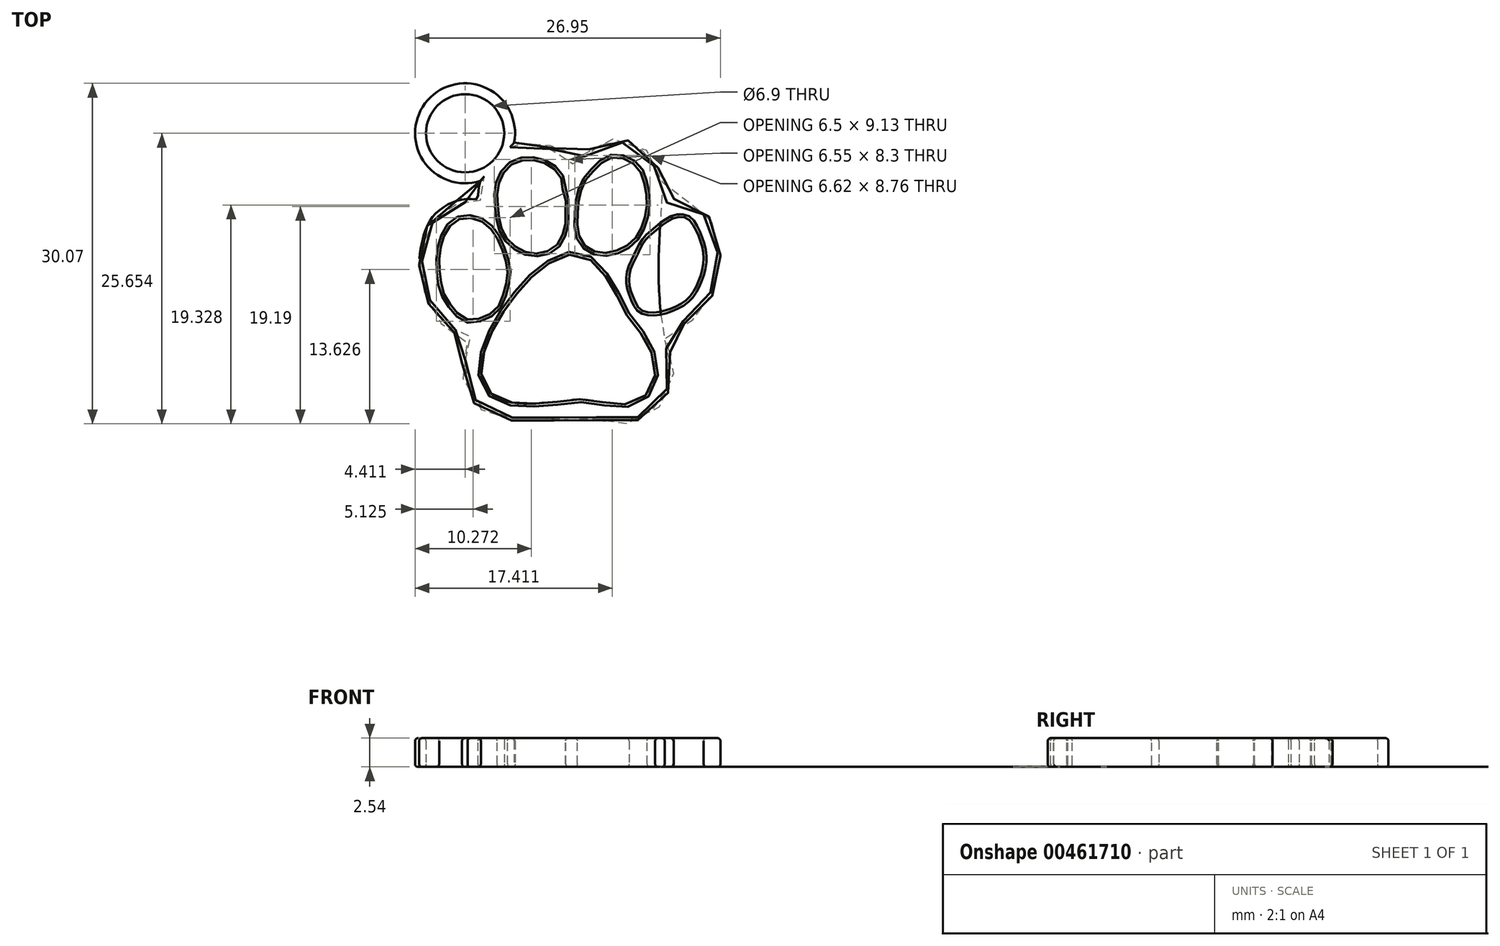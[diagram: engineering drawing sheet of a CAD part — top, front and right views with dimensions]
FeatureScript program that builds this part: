
annotation { "Feature Type Name" : "Feature", "Feature Type Description" : "" }
export const myFeature = defineFeature(function(context is Context, id is Id, definition is map)
    precondition{}
    {
        {
            var Q0;
            Q0=qCreatedBy(makeId("Top.planeOp"),FACE);
            var sketch = newSketch(context, id + "F0", { "sketchPlane" : qUnion([Q0])});
            skPoint(sketch, "E0.middle", {"position": v(0, 0) * mm});
            skFitSpline(sketch, "E1", {"points": [v(0.8, 9.25) * mm, v(1.85, 10.08) * mm, v(3.3, 10.95) * mm, v(5.35, 11.07) * mm, v(7.02, 10.27) * mm, v(7.95, 9.06) * mm, v(8.63, 7.14) * mm, v(8.78, 6) * mm, v(8.78, 5.81) * mm, v(8.94, 5.81) * mm, v(10.18, 5.86) * mm, v(11.2, 5.64) * mm, v(12.22, 4.87) * mm, v(13.49, 2.43) * mm, v(13.55, -0.42) * mm, v(12.76, -3.12) * mm, v(11.25, -4.79) * mm, v(8.86, -5.83) * mm, v(8.78, -5.89) * mm, v(8.75, -6) * mm, v(8.78, -6.12) * mm, v(9.33, -8) * mm, v(9.43, -10.3) * mm, v(8.29, -12.48) * mm, v(7.72, -12.95) * mm, v(5.95, -13.83) * mm, v(4.02, -13.93) * mm, v(2.72, -13.67) * mm, v(1.9, -13.47) * mm, v(1.68, -13.47) * mm, v(0.61, -13.46) * mm, v(-0.31, -13.62) * mm, v(-1.11, -13.7) * mm, v(-1.96, -13.74) * mm, v(-3.44, -13.74) * mm, v(-4.2, -13.74) * mm, v(-5.71, -13.5) * mm, v(-7.8, -12.45) * mm, v(-8.8, -10.88) * mm, v(-9.12, -9.52) * mm, v(-9, -7.92) * mm, v(-8.68, -6.67) * mm, v(-8.66, -6.47) * mm, v(-8.66, -6.36) * mm, v(-8.88, -6.29) * mm, v(-10.37, -5.63) * mm, v(-11.93, -3.75) * mm, v(-12.87, -0.69) * mm, v(-12.76, 1.66) * mm, v(-12.09, 3.74) * mm, v(-11.12, 4.89) * mm, v(-9.37, 5.76) * mm, v(-7.97, 5.85) * mm, v(-7.85, 5.85) * mm, v(-7.73, 5.91) * mm, v(-7.73, 6.16) * mm, v(-7.54, 7.43) * mm, v(-6.9, 9.1) * mm, v(-5.5, 10.36) * mm, v(-3.78, 11) * mm, v(-1.74, 10.72) * mm, v(-0.62, 10.12) * mm, v(0.43, 9.4) * mm, v(0.57, 9.28) * mm, v(0.64, 9.23) * mm, v(0.7, 9.22) * mm, v(0.74, 9.22) * mm, v(0.8, 9.25) * mm]});
            skFitSpline(sketch, "E2", {"points": [v(0.35, 0.93) * mm, v(1.28, 0.88) * mm, v(2.22, 0.47) * mm, v(3.36, -0.73) * mm, v(4.4, -2.4) * mm, v(5.08, -3.75) * mm, v(5.65, -4.79) * mm, v(6.43, -5.78) * mm, v(7, -6.35) * mm, v(7.32, -6.92) * mm, v(7.84, -8.74) * mm, v(7.79, -10.35) * mm, v(6.9, -11.6) * mm, v(5.63, -12.17) * mm, v(4.66, -12.3) * mm, v(3.2, -12.05) * mm, v(2.13, -11.86) * mm, v(1.32, -11.82) * mm, v(0.34, -11.86) * mm, v(-0.52, -12.03) * mm, v(-1.47, -12.1) * mm, v(-2.89, -12.2) * mm, v(-4.58, -12.13) * mm, v(-6.33, -11.52) * mm, v(-7.2, -10.45) * mm, v(-7.48, -9.1) * mm, v(-7.07, -7.27) * mm, v(-6.13, -5.12) * mm, v(-4.5, -2.75) * mm, v(-2.68, -0.75) * mm, v(-0.8, 0.6) * mm, v(-0.27, 0.81) * mm, v(0.14, 0.88) * mm, v(0.35, 0.93) * mm]});
            skFitSpline(sketch, "E3", {"points": [v(9.5, 4.18) * mm, v(10.39, 4.26) * mm, v(11.07, 3.86) * mm, v(11.83, 2.37) * mm, v(12.2, 0.65) * mm, v(11.91, -0.92) * mm, v(11.03, -2.68) * mm, v(9.43, -3.77) * mm, v(7.54, -4.17) * mm, v(6.54, -3.85) * mm, v(6.14, -3.16) * mm, v(5.7, -2.04) * mm, v(5.7, -0.48) * mm, v(6.26, 0.77) * mm, v(6.94, 2.1) * mm, v(8.26, 3.33) * mm, v(8.94, 3.86) * mm, v(9.2, 4) * mm, v(9.38, 4.1) * mm, v(9.46, 4.14) * mm, v(9.5, 4.18) * mm]});
            skFitSpline(sketch, "E4", {"points": [v(1.79, 7.53) * mm, v(3, 8.88) * mm, v(4.48, 9.56) * mm, v(5.95, 9.02) * mm, v(6.7, 8.08) * mm, v(7.17, 6.05) * mm, v(7.06, 4.44) * mm, v(6.28, 2.57) * mm, v(5.14, 1.58) * mm, v(3.58, 1.11) * mm, v(2.12, 1.42) * mm, v(1.18, 2.62) * mm, v(1.08, 4.8) * mm, v(1.23, 6.16) * mm, v(1.54, 7.06) * mm, v(1.69, 7.35) * mm, v(1.79, 7.53) * mm]});
            skFitSpline(sketch, "E5", {"points": [v(-4.76, 8.9) * mm, v(-3.93, 9.25) * mm, v(-2.57, 9.25) * mm, v(-1.43, 8.8) * mm, v(-0.6, 8.07) * mm, v(-0.28, 7.3) * mm, v(-0.23, 6.62) * mm, v(0, 5.81) * mm, v(0, 5.1) * mm, v(0, 3.76) * mm, v(-0.23, 2.77) * mm, v(-0.8, 1.78) * mm, v(-2.16, 1.1) * mm, v(-3.72, 1.26) * mm, v(-5.12, 2.3) * mm, v(-5.7, 3.4) * mm, v(-5.95, 5) * mm, v(-6, 6.67) * mm, v(-5.6, 7.97) * mm, v(-5.12, 8.6) * mm, v(-4.93, 8.74) * mm, v(-4.76, 8.9) * mm]});
            skFitSpline(sketch, "E6", {"points": [v(-10.2, 3.48) * mm, v(-9.4, 4.08) * mm, v(-7.92, 4.08) * mm, v(-6.5, 3.14) * mm, v(-5.55, 1.25) * mm, v(-5.12, -0.69) * mm, v(-5.42, -2.33) * mm, v(-6.03, -3.75) * mm, v(-7.07, -4.48) * mm, v(-8.66, -4.79) * mm, v(-9.94, -3.75) * mm, v(-10.82, -2.26) * mm, v(-11.15, 0) * mm, v(-11.02, 1.65) * mm, v(-10.56, 2.98) * mm, v(-10.4, 3.2) * mm, v(-10.2, 3.48) * mm]});
            skArc(sketch, "E7", {"start": v(-4.53, 10.84) * mm, "mid": v(-12.17, 14.6) * mm, "end": v(-7.53, 7.46) * mm});
            skCircle(sketch, "E8", {"center": v(-8.87, 11.66) * mm, "radius": 3.45 * mm});
            skSolve(sketch);
        }
        {
            var Q0;
            Q0 = qSketchRegion(id + "F0", true);
            extrude(context, id + "F1", {"entities" : qUnion([Q0]), "depth" : 2.54 * mm});
        }
        {
            var Q0;
            Q0=makeQuery(id+"F1.opExtrude","CAP_FACE",FACE,{"disambiguationData":[OSD([sQuery(id+"F0.wireOp",EDGE,"E1"),sQuery(id+"F0.wireOp",EDGE,"E2"),sQuery(id+"F0.wireOp",EDGE,"E3"),sQuery(id+"F0.wireOp",EDGE,"E4"),sQuery(id+"F0.wireOp",EDGE,"E5"),sQuery(id+"F0.wireOp",EDGE,"E6"),sQuery(id+"F0.wireOp",EDGE,"E7"),sQuery(id+"F0.wireOp",EDGE,"E8")])],"isStart":false});
            var Q1;
            Q1=makeQuery(id+"F1.opExtrude","CAP_FACE",FACE,{"disambiguationData":[OSD([sQuery(id+"F0.wireOp",EDGE,"E1"),sQuery(id+"F0.wireOp",EDGE,"E2"),sQuery(id+"F0.wireOp",EDGE,"E3"),sQuery(id+"F0.wireOp",EDGE,"E4"),sQuery(id+"F0.wireOp",EDGE,"E5"),sQuery(id+"F0.wireOp",EDGE,"E6"),sQuery(id+"F0.wireOp",EDGE,"E7"),sQuery(id+"F0.wireOp",EDGE,"E8")])],"isStart":true});
            fillet(context, id + "F2", {"entities" : qUnion([Q0, Q1]), "radius" : 0.25 * mm, "tangentPropagation" : true, "allowEdgeOverflow" : false});
        }
    });
